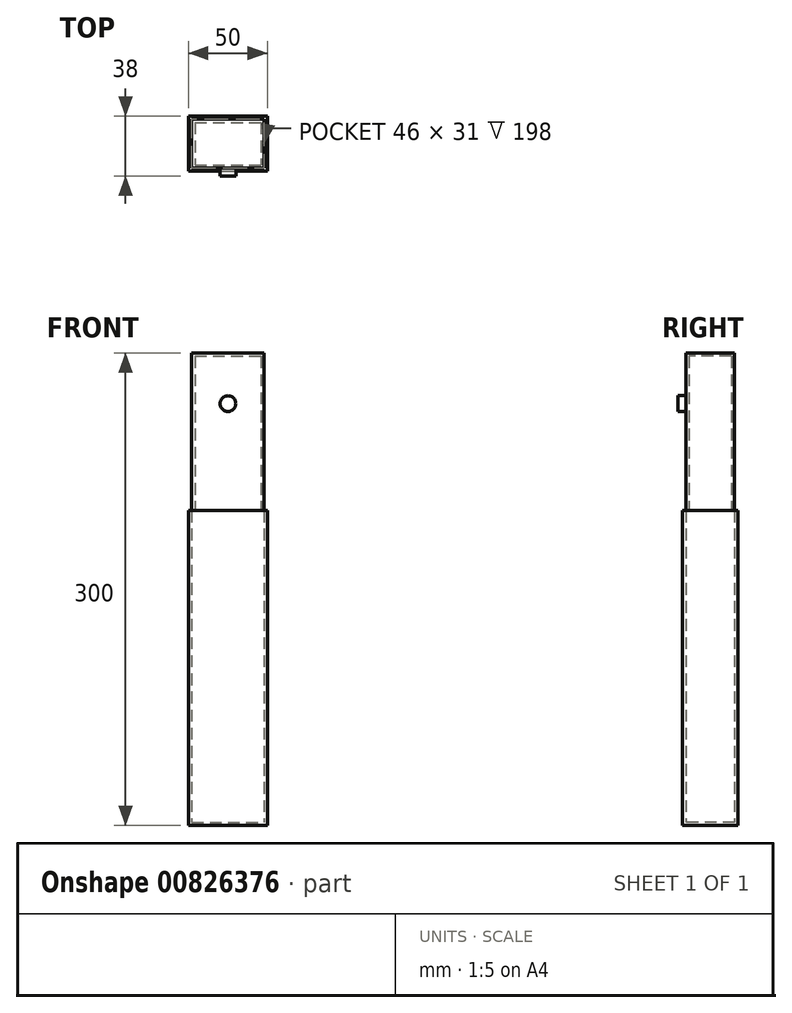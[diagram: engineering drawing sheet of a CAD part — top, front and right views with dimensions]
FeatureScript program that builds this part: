
annotation { "Feature Type Name" : "Feature", "Feature Type Description" : "" }
export const myFeature = defineFeature(function(context is Context, id is Id, definition is map)
    precondition{}
    {
        {
            var Q0;
            Q0=qCreatedBy(makeId("Top.planeOp"),FACE);
            var sketch = newSketch(context, id + "F0", { "sketchPlane" : qUnion([Q0])});
            skLineSegment(sketch, "E0.bottom", {"start": v(-25, 50) * mm, "end": v(25, 50) * mm});
            skLineSegment(sketch, "E0.top", {"start": v(-25, 0) * mm, "end": v(25, 0) * mm});
            skLineSegment(sketch, "E0.left", {"start": v(-25, 50) * mm, "end": v(-25, 0) * mm});
            skLineSegment(sketch, "E0.right", {"start": v(25, 50) * mm, "end": v(25, 0) * mm});
            skLineSegment(sketch, "E1.top", {"start": v(-25, 15) * mm, "end": v(25, 15) * mm});
            skLineSegment(sketch, "E1.left", {"start": v(-25, 50) * mm, "end": v(-25, 15) * mm});
            skLineSegment(sketch, "E1.right", {"start": v(25, 50) * mm, "end": v(25, 15) * mm});
            skSolve(sketch);
        }
        {
            var Q0;
            {var subQ0=sQuery(id+"F0.wireOp",EDGE,"E0.bottom");Q0=makeQuery(id+"F0.imprint","IMPRINT",FACE,{"disambiguationData":[TD([[makeQuery(id+"F0.imprint","IMPRINT",EDGE,{"derivedFrom":subQ0}),-1.0]])]});}
            extrude(context, id + "F1", {"entities" : qUnion([Q0]), "depth" : 200 * mm, "offsetDistance" : 25 * mm});
        }
        {
            var Q0;
            Q0=makeQuery(id+"F1.opExtrude","CAP_FACE",FACE,{"disambiguationData":[OSD([sQuery(id+"F0.wireOp",EDGE,"E0.bottom"),sQuery(id+"F0.wireOp",EDGE,"E0.left"),sQuery(id+"F0.wireOp",EDGE,"E0.right"),sQuery(id+"F0.wireOp",EDGE,"E1.top")])],"isStart":false});
            shell(context, id + "F2", {"entities" : qUnion([Q0]), "thickness" : 2 * mm});
        }
        {
            var Q0;
            Q0=makeQuery(id+"F1.opExtrude","CAP_FACE",FACE,{"disambiguationData":[OSD([sQuery(id+"F0.wireOp",EDGE,"E0.bottom"),sQuery(id+"F0.wireOp",EDGE,"E0.left"),sQuery(id+"F0.wireOp",EDGE,"E0.right"),sQuery(id+"F0.wireOp",EDGE,"E1.top")])],"isStart":false});
            var sketch = newSketch(context, id + "F3", { "sketchPlane" : qUnion([Q0])});
            skSolve(sketch);
        }
        {
            var Q0;
            Q0 = qSketchRegion(id + "F3", true);
            var Q1;
            {var subQ0=sQuery(id+"F0.wireOp",EDGE,"E0.bottom");Q1=makeQuery(id+"F3.imprint","IMPRINT",FACE,{"disambiguationData":[TD([[makeQuery(id+"F3.imprint","IMPRINT",EDGE,{"derivedFrom":makeQuery(id+"F2.opShell","OFFSET_EDGE",EDGE,{"disambiguationData":[OSD([subQ0]),TDD([makeQuery(id+"F1.opExtrude","CAP_EDGE",EDGE,{"disambiguationData":[OSD([subQ0])],"isStart":false})])]})}),-1.0]])]});}
            extrude(context, id + "F4", {"entities" : qUnion([Q0, Q1]), "depth" : 100 * mm, "offsetDistance" : 25 * mm});
        }
        {
            var Q0;
            Q0=makeQuery(id+"F4.opExtrude","CAP_FACE",FACE,{"disambiguationData":[OSD([sQuery(id+"F0.wireOp",EDGE,"E0.bottom"),sQuery(id+"F0.wireOp",EDGE,"E0.left"),sQuery(id+"F0.wireOp",EDGE,"E0.right"),sQuery(id+"F0.wireOp",EDGE,"E1.top")])],"isStart":true});
            shell(context, id + "F5", {"entities" : qUnion([Q0]), "thickness" : 2 * mm});
        }
        {
            var Q0;
            Q0=makeQuery(id+"F4.opExtrude","SWEPT_FACE",FACE,{"disambiguationData":[OSD([sQuery(id+"F0.wireOp",EDGE,"E1.top")])]});
            var sketch = newSketch(context, id + "F6", { "sketchPlane" : qUnion([Q0])});
            skCircle(sketch, "E2", {"center": v(0, 267.89) * mm, "radius": 5 * mm});
            skSolve(sketch);
        }
        {
            var Q0;
            Q0=makeQuery(id+"F6.imprint","IMPRINT",FACE,{"disambiguationData":[TD([[makeQuery(id+"F6.imprint","IMPRINT",EDGE,{"derivedFrom":sQuery(id+"F6.wireOp",EDGE,"E2")}),1.0]])]});
            extrude(context, id + "F7", {"entities" : qUnion([Q0]), "operationType" : NewBodyOperationType.ADD, "depth" : 5 * mm, "offsetDistance" : 25 * mm});
        }
    });
